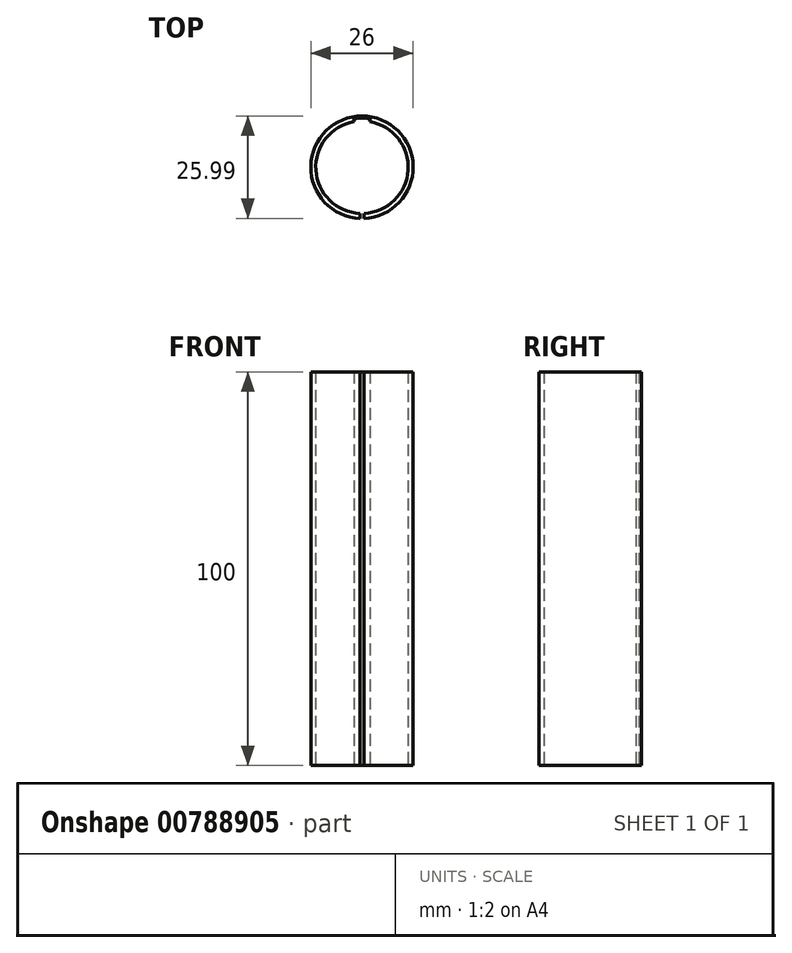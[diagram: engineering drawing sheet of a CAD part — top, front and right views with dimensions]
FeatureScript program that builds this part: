
annotation { "Feature Type Name" : "Feature", "Feature Type Description" : "" }
export const myFeature = defineFeature(function(context is Context, id is Id, definition is map)
    precondition{}
    {
        {
            var Q0;
            Q0=qCreatedBy(makeId("Top.planeOp"),FACE);
            var sketch = newSketch(context, id + "F0", { "sketchPlane" : qUnion([Q0])});
            skCircle(sketch, "E0", {"center": v(0, 0) * mm, "radius": 11.75 * mm});
            skCircle(sketch, "E1", {"center": v(0, 0) * mm, "radius": 13 * mm});
            skArc(sketch, "E2", {"start": v(2, 12.34) * mm, "mid": v(0, 12.5) * mm, "end": v(-2, 12.34) * mm});
            skLineSegment(sketch, "E3", {"start": v(-2, 12.34) * mm, "end": v(-2, 11.58) * mm});
            skLineSegment(sketch, "E4", {"start": v(2, 12.34) * mm, "end": v(2, 11.58) * mm});
            skLineSegment(sketch, "E5", {"start": v(-0.5, -11.74) * mm, "end": v(-0.5, -13) * mm});
            skLineSegment(sketch, "E6", {"start": v(0.5, -11.74) * mm, "end": v(0.5, -13) * mm});
            skSolve(sketch);
        }
        {
            var Q0;
            Q0=makeQuery(id+"F0.imprint","IMPRINT",FACE,{"disambiguationData":[TD([[makeQuery(id+"F0.imprint","IMPRINT",EDGE,{"derivedFrom":sQuery(id+"F0.wireOp",EDGE,"E2")}),-1.0]])]});
            extrude(context, id + "F1", {"entities" : qUnion([Q0]), "depth" : 100 * mm, "offsetDistance" : 25 * mm});
        }
    });
